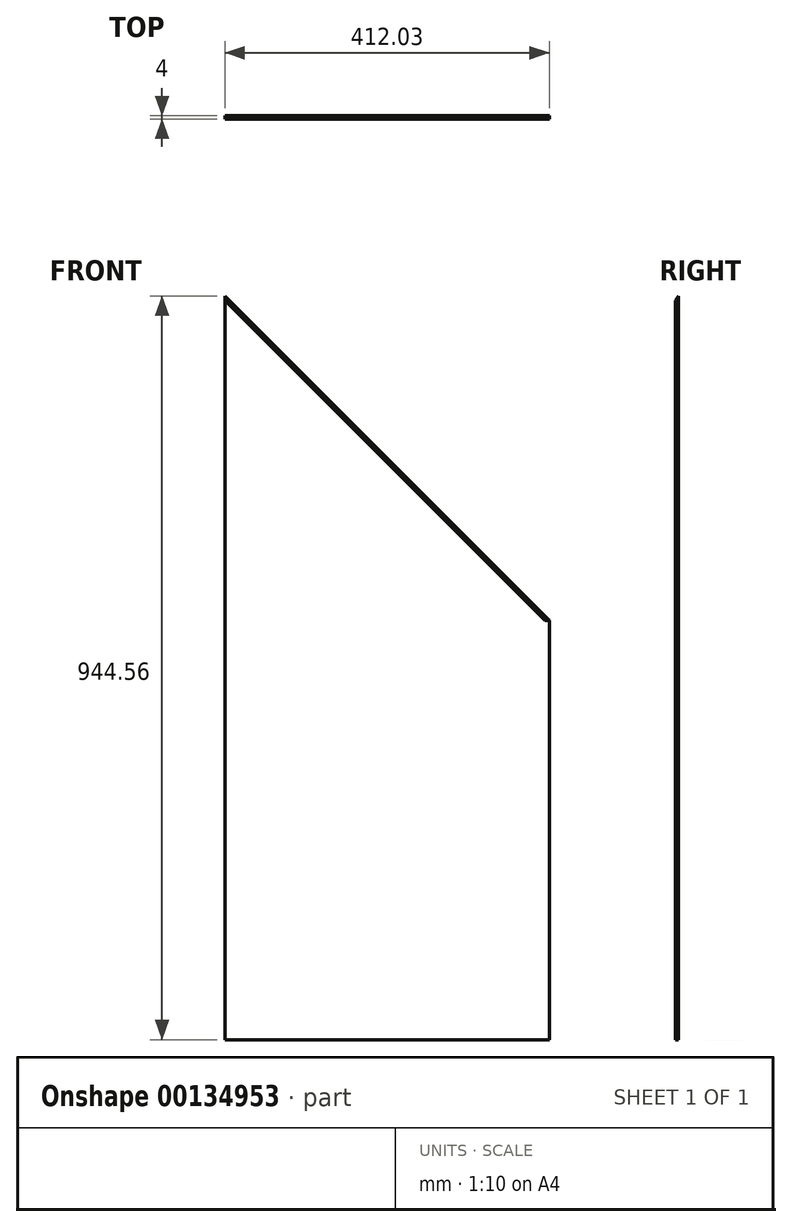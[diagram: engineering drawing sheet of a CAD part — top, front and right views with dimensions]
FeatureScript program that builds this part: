
annotation { "Feature Type Name" : "Feature", "Feature Type Description" : "" }
export const myFeature = defineFeature(function(context is Context, id is Id, definition is map)
    precondition{}
    {
        {
            var Q0;
            Q0=qCreatedBy(makeId("Front.planeOp"),FACE);
            var sketch = newSketch(context, id + "F0", { "sketchPlane" : qUnion([Q0])});
            skLineSegment(sketch, "E0", {"start": v(0, 0) * mm, "end": v(412.03, 0) * mm});
            skLineSegment(sketch, "E1", {"start": v(412.03, 0) * mm, "end": v(412.03, 532.53) * mm});
            skLineSegment(sketch, "E2", {"start": v(412.03, 532.53) * mm, "end": v(0, 944.56) * mm});
            skLineSegment(sketch, "E3", {"start": v(0, 944.56) * mm, "end": v(0, 0) * mm});
            skSolve(sketch);
        }
        {
            var Q0;
            Q0=makeQuery(id+"F0.imprint","IMPRINT",FACE,{"disambiguationData":[TD([[makeQuery(id+"F0.imprint","IMPRINT",EDGE,{"derivedFrom":sQuery(id+"F0.wireOp",EDGE,"E0")}),1.0]])]});
            extrude(context, id + "F1", {"entities" : qUnion([Q0]), "depth" : 4 * mm});
        }
        {
            var Q0;
            Q0=makeQuery(id+"F1.opExtrude","CAP_EDGE",EDGE,{"disambiguationData":[OSD([sQuery(id+"F0.wireOp",EDGE,"E2")])],"isStart":false});
            chamfer(context, id + "F2", {"entities" : qUnion([Q0]), "width" : 4 * mm, "tangentPropagation" : true});
        }
        {
            var Q0;
            Q0=makeQuery(id+"F1.opExtrude","SWEPT_FACE",FACE,{"disambiguationData":[OSD([sQuery(id+"F0.wireOp",EDGE,"E1")])]});
            var sketch = newSketch(context, id + "F3", { "sketchPlane" : qUnion([Q0])});
            skLineSegment(sketch, "E4.bottom", {"start": v(-4, 526.87) * mm, "end": v(0, 526.87) * mm});
            skLineSegment(sketch, "E4.top", {"start": v(-4, 532.53) * mm, "end": v(0, 532.53) * mm});
            skLineSegment(sketch, "E4.left", {"start": v(-4, 526.87) * mm, "end": v(-4, 532.53) * mm});
            skLineSegment(sketch, "E4.right", {"start": v(0, 526.87) * mm, "end": v(0, 532.53) * mm});
            skSolve(sketch);
        }
        {
            var Q0;
            Q0=makeQuery(id+"F3.imprint","IMPRINT",FACE,{"disambiguationData":[TD([[makeQuery(id+"F3.imprint","IMPRINT",EDGE,{"derivedFrom":sQuery(id+"F3.wireOp",EDGE,"E4.top")}),-1.0]])]});
            extrude(context, id + "F4", {"entities" : qUnion([Q0]), "operationType" : NewBodyOperationType.ADD, "oppositeDirection" : true, "depth" : 25 * mm});
        }
    });
